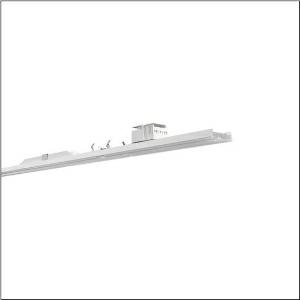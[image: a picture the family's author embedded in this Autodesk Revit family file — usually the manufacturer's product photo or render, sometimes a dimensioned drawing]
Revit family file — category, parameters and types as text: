
# Revit family: licross_r__11_recessed_mo_51tl12dn59xf_d942
name_source: partatom
category: Lighting Fixtures
units: mm (PartAtom-declared; Revit-internal decimal feet)

## family parameters
Cut with Voids When Loaded = No
Host = Face
Light Source = No
Part Type = Normal
Room Calculation Point = No
Round Connector Dimension = Use Diameter
Shared = No

## types (1)
- --- (1 x LED, 9070 lm, 55.4 W, 5000K)
    Apparent Load = 55 VA
    CIE Flux Codes = 67 92 99 100 100
    Color Rendering = 80
    Color Temperature = 5000K
    Default Elevation = 1800 mm
    Description = Licross® 11 Recessed MOluminaire insert, length: 1.500mm, width: 66mm, height: 67mm, LED rated luminous flux: 9.070lm, light colour: 850, control gear: DALI 2, control gear: ECG DALI, with plug, 5-pole, with phase selection, mains connection: 220..240V, AC, 50/60Hz, halogen-free wiring, primary optical cover: cover, of PMMA, light emission: direct distribution, protection rating (complete): IP40, insulation class (complete): insulation class I (protective earthing), certification: CE, ENEC, VDE, protection symbol: D if used in an environment without relevant dust loads with corresponding accessories, permissible ambient temperature for indoor applications: -25..+40°C, reducing of maximum allowable ambient temperature of 5°C with ceiling mounting, corresponds to IFS (International Featured Standards) requirements for safety and quality in the food industry, packaging unit: 1 piece
    Height = 58 mm
    Lamp = 1 x LED
    Lamp Light Flux = 9070 lm
    Lamp Power = 55.4 W
    Lamp count = 1
    Length = 1500 mm
    Luminous efficacy = 164 lm/W
    Manufacturer = Siteco
    ModVariant = No
    Model = 51TL12DN59XF
    Mounting Place = Ceiling
    Mounting Type = Pendant
    Number of Poles = 1
    OnlyDefault = Yes
    Power Factor = 1
    Product Name = Licross® 11 Recessed MO
    Product group = luminaire insert
    ProductGroupID = 902
    Protection Class = Protection class I
    Protection Degree = IP 40
    RLX_Detail_Level = 1
    RlxData = <blob elided: 22253 chars, md5=6b17abb2>
    Socket = socket
    Standby Power = 0 W
    System Light Flux = 9070 lm
    System Power = 55 W
    Type Comments = factory setting: luminous flux: 100 % | dim-lin: 254 | 365 mA
    Type Image = l_1266722.jpg
    URL = http://relux.com
    VarID = @adj_068269
    Voltage = 0 V
    Weight = 0.00 kg
    Width = 66 mm

## geometry (parser evidence)
native form markers: Blend x4, Sweep x10
no freeform markers — native parametric forms only
